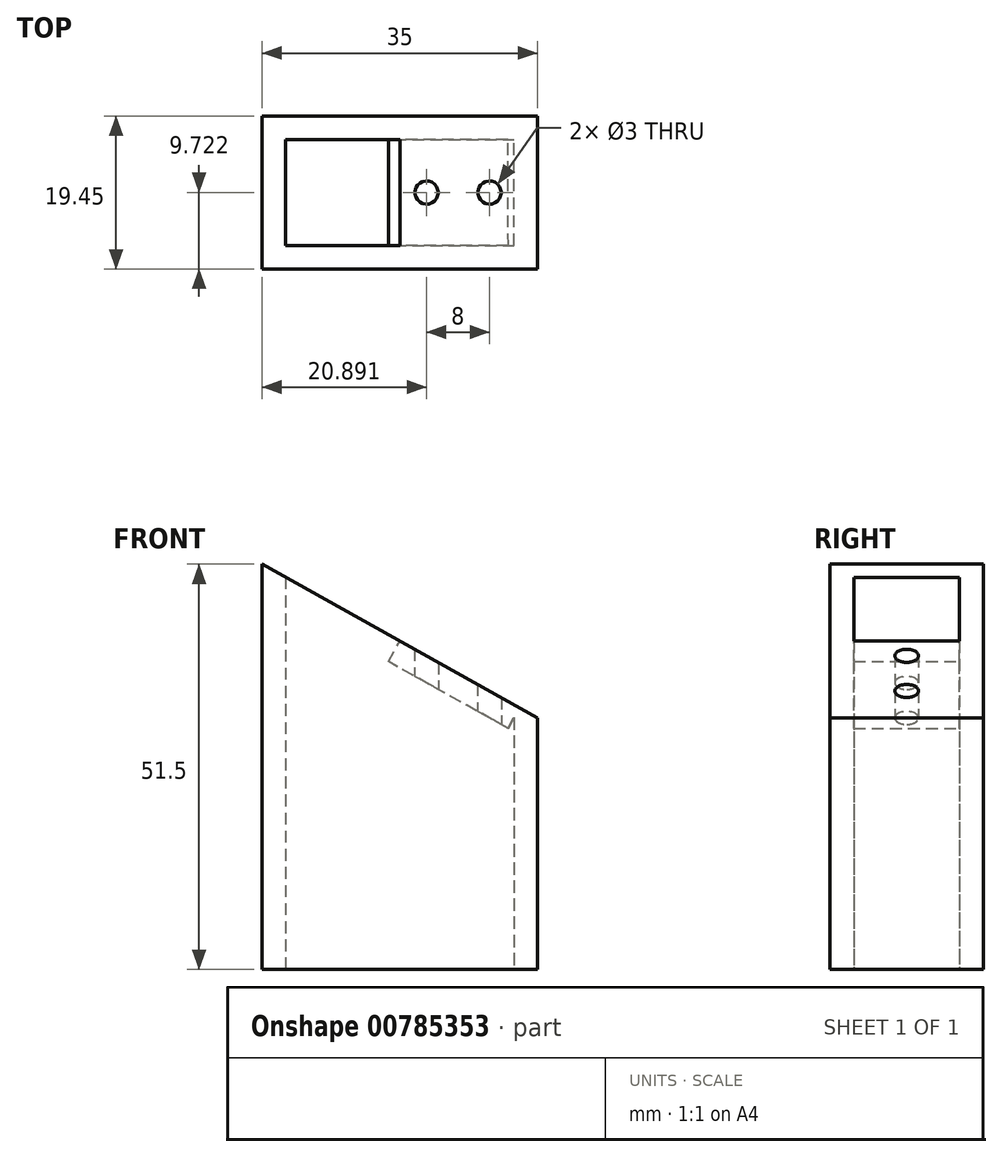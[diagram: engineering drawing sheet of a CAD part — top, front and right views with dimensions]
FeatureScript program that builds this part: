
annotation { "Feature Type Name" : "Feature", "Feature Type Description" : "" }
export const myFeature = defineFeature(function(context is Context, id is Id, definition is map)
    precondition{}
    {
        {
            var Q0;
            Q0=qCreatedBy(makeId("Top.planeOp"),FACE);
            var sketch = newSketch(context, id + "F0", { "sketchPlane" : qUnion([Q0])});
            skLineSegment(sketch, "E0.bottom", {"start": v(-52.24, 6.99) * mm, "end": v(-23.24, 6.99) * mm});
            skLineSegment(sketch, "E0.top", {"start": v(-52.24, -6.46) * mm, "end": v(-23.24, -6.46) * mm});
            skLineSegment(sketch, "E0.left", {"start": v(-52.24, 6.99) * mm, "end": v(-52.24, -6.46) * mm});
            skLineSegment(sketch, "E0.right", {"start": v(-23.24, 6.99) * mm, "end": v(-23.24, -6.46) * mm});
            skLineSegment(sketch, "E1.0", {"start": v(-55.24, 9.99) * mm, "end": v(-20.24, 9.99) * mm});
            skLineSegment(sketch, "E1.1", {"start": v(-55.24, 9.99) * mm, "end": v(-55.24, -9.46) * mm});
            skLineSegment(sketch, "E1.2", {"start": v(-55.24, -9.46) * mm, "end": v(-20.24, -9.46) * mm});
            skLineSegment(sketch, "E1.3", {"start": v(-20.24, 9.99) * mm, "end": v(-20.24, -9.46) * mm});
            skSolve(sketch);
        }
        {
            var Q0;
            Q0=makeQuery(id+"F0.imprint","IMPRINT",FACE,{"disambiguationData":[TD([[makeQuery(id+"F0.imprint","IMPRINT",EDGE,{"derivedFrom":sQuery(id+"F0.wireOp",EDGE,"E0.bottom")}),1.0]])]});
            extrude(context, id + "F1", {"entities" : qUnion([Q0]), "depth" : 51.5 * mm, "offsetDistance" : 25 * mm});
        }
        {
            var Q0;
            Q0=makeQuery(id+"F1.opExtrude","SWEPT_FACE",FACE,{"disambiguationData":[OSD([sQuery(id+"F0.wireOp",EDGE,"E1.2")])]});
            var sketch = newSketch(context, id + "F2", { "sketchPlane" : qUnion([Q0])});
            skLineSegment(sketch, "E2.0", {"start": v(-55.24, 51.5) * mm, "end": v(-55.24, 0) * mm});
            skLineSegment(sketch, "E2.1", {"start": v(-20.24, 51.5) * mm, "end": v(-20.24, 0) * mm});
            skLineSegment(sketch, "E3", {"start": v(-55.24, 51.5) * mm, "end": v(-20.24, 32) * mm});
            skSolve(sketch);
        }
        {
            var Q0;
            {var subQ2=sQuery(id+"F2.wireOp",EDGE,"E3");Q0=makeQuery(id+"F2.imprint","IMPRINT",FACE,{"disambiguationData":[TD([[makeQuery(id+"F2.imprint","IMPRINT",EDGE,{"derivedFrom":subQ2}),1.0]])]});}
            extrude(context, id + "F3", {"entities" : qUnion([Q0]), "operationType" : NewBodyOperationType.REMOVE, "oppositeDirection" : true, "depth" : 25 * mm, "offsetDistance" : 25 * mm});
        }
        {
            var Q0;
            Q0=makeQuery(id+"F3.boolean.opBoolean","COPY",FACE,{"derivedFrom":makeQuery(id+"F3.opExtrude","SWEPT_FACE",FACE,{"disambiguationData":[OSD([sQuery(id+"F2.wireOp",EDGE,"E3")])]})});
            var sketch = newSketch(context, id + "F4", { "sketchPlane" : qUnion([Q0])});
            skLineSegment(sketch, "E4.0", {"start": v(-36.7, 6.99) * mm, "end": v(-69.89, 6.99) * mm});
            skLineSegment(sketch, "E4.1", {"start": v(-69.89, -6.46) * mm, "end": v(-69.89, 6.99) * mm});
            skLineSegment(sketch, "E4.2", {"start": v(-36.7, -6.46) * mm, "end": v(-69.89, -6.46) * mm});
            skLineSegment(sketch, "E5", {"start": v(-53.3, 6.99) * mm, "end": v(-53.3, -6.46) * mm, "construction": true});
            skLineSegment(sketch, "E6.bottom", {"start": v(-53.3, -6.46) * mm, "end": v(-35.85, -6.46) * mm});
            skLineSegment(sketch, "E6.top", {"start": v(-53.3, 6.99) * mm, "end": v(-35.9, 6.99) * mm});
            skLineSegment(sketch, "E6.left", {"start": v(-53.3, -6.46) * mm, "end": v(-53.3, 6.99) * mm});
            skCircle(sketch, "E7", {"center": v(-41.72, 0) * mm, "radius": 1.5 * mm});
            skCircle(sketch, "E8", {"center": v(-49.28, 0.26) * mm, "radius": 1.5 * mm});
            skPoint(sketch, "E8.centerSnap0", {"position": v(-53.3, 0.26) * mm});
            skLineSegment(sketch, "E9", {"start": v(-36.7, -6.46) * mm, "end": v(-36.7, 6.99) * mm});
            skLineSegment(sketch, "E10", {"start": v(-35.85, -6.46) * mm, "end": v(-35.9, 6.99) * mm});
            skSolve(sketch);
        }
        {
            var Q0;
            {var subQ0=sQuery(id+"F4.wireOp",EDGE,"E6.left");Q0=makeQuery(id+"F4.imprint","IMPRINT",FACE,{"disambiguationData":[TD([[makeQuery(id+"F4.imprint","IMPRINT",EDGE,{"derivedFrom":subQ0}),-1.0]])]});}
            var Q1;
            {var subQ0=sQuery(id+"F4.wireOp",EDGE,"E9");Q1=makeQuery(id+"F4.imprint","IMPRINT",FACE,{"disambiguationData":[TD([[makeQuery(id+"F4.imprint","IMPRINT",EDGE,{"derivedFrom":subQ0}),-1.0]])]});}
            var Q2;
            Q2=makeQuery(id+"F4.imprint","IMPRINT",FACE,{"disambiguationData":[TD([[makeQuery(id+"F4.imprint","IMPRINT",EDGE,{"derivedFrom":sQuery(id+"F4.wireOp",EDGE,"E7")}),1.0]])]});
            var Q3;
            Q3=makeQuery(id+"F4.imprint","IMPRINT",FACE,{"disambiguationData":[TD([[makeQuery(id+"F4.imprint","IMPRINT",EDGE,{"derivedFrom":sQuery(id+"F4.wireOp",EDGE,"E8")}),1.0]])]});
            extrude(context, id + "F5", {"entities" : qUnion([Q0, Q1, Q2, Q3]), "operationType" : NewBodyOperationType.ADD, "oppositeDirection" : true, "depth" : 3 * mm, "offsetDistance" : 25 * mm});
        }
        {
            var Q0;
            Q0=makeQuery(id+"F1.opExtrude","CAP_FACE",FACE,{"disambiguationData":[OSD([sQuery(id+"F0.wireOp",EDGE,"E0.bottom"),sQuery(id+"F0.wireOp",EDGE,"E0.top"),sQuery(id+"F0.wireOp",EDGE,"E0.left"),sQuery(id+"F0.wireOp",EDGE,"E0.right"),sQuery(id+"F0.wireOp",EDGE,"E1.0"),sQuery(id+"F0.wireOp",EDGE,"E1.1"),sQuery(id+"F0.wireOp",EDGE,"E1.2"),sQuery(id+"F0.wireOp",EDGE,"E1.3")])],"isStart":true});
            var sketch = newSketch(context, id + "F6", { "sketchPlane" : qUnion([Q0])});
            skLineSegment(sketch, "E11.0", {"start": v(-24, -6.99) * mm, "end": v(-39.2, -6.99) * mm});
            skLineSegment(sketch, "E11.1", {"start": v(-39.2, 6.46) * mm, "end": v(-39.2, -6.99) * mm});
            skLineSegment(sketch, "E11.2", {"start": v(-23.97, 6.46) * mm, "end": v(-39.2, 6.46) * mm});
            skLineSegment(sketch, "E11.3", {"start": v(-23.97, 6.46) * mm, "end": v(-24, -6.99) * mm});
            skPoint(sketch, "E12.centerSnap0", {"position": v(-39.2, -0.26) * mm});
            skCircle(sketch, "E13", {"center": v(-34.35, -0.26) * mm, "radius": 1.5 * mm});
            skCircle(sketch, "E14", {"center": v(-26.35, -0.26) * mm, "radius": 1.5 * mm});
            skPoint(sketch, "E14.centerSnap0", {"position": v(-23.99, -0.26) * mm});
            skSolve(sketch);
        }
        {
            var Q0;
            Q0=makeQuery(id+"F6.imprint","IMPRINT",FACE,{"disambiguationData":[TD([[makeQuery(id+"F6.imprint","IMPRINT",EDGE,{"derivedFrom":sQuery(id+"F6.wireOp",EDGE,"E14")}),1.0]])]});
            var Q1;
            Q1=makeQuery(id+"F6.imprint","IMPRINT",FACE,{"disambiguationData":[TD([[makeQuery(id+"F6.imprint","IMPRINT",EDGE,{"derivedFrom":sQuery(id+"F6.wireOp",EDGE,"E13")}),1.0]])]});
            extrude(context, id + "F7", {"entities" : qUnion([Q0, Q1]), "operationType" : NewBodyOperationType.REMOVE, "oppositeDirection" : true, "depth" : 46.3 * mm, "offsetDistance" : 25 * mm});
        }
    });
